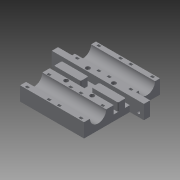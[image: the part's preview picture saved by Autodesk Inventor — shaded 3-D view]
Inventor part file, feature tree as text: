
AUTODESK INVENTOR PART (.ipt)
format: ipt  version: 2015 SP2 (Build 190223200, 223)  size: 303,616 bytes
history: native  units: mm
features: sketch x8, extrude x6, hole x2, fillet x1
ambient origin geometry x8: Origin, YZ Plane, XZ Plane, XY Plane, X Axis, Y Axis, Z Axis, Center Point
bodies: Solid1 (feature_tree)
feature tree (17):
  extrude  "Extrusion1"  Depth=70.0mm
  extrude  "Extrusion2"  Depth=13.0mm
  extrude  "Extrusion3"  Depth=22.0mm
  hole  "Hole1"  [1 undecoded]
  extrude  "Extrusion4"  Depth=45.0mm
  extrude  "Extrusion5"  Depth=13.0mm TaperAngle=0.0deg
  hole  "Hole2"  [1 undecoded]
  extrude  "Extrusion6"  Depth=3.75mm
  fillet  "Fillet1"  Radius=23.0mm
  sketch  "Sketch1"  dims[d0=85.0mm d1=70.0mm]
  sketch  "Sketch2"  dims[d2=13.0mm d3=0.0mm d4=13.0mm]
  sketch  "Sketch3"  dims[d5=5.75mm d6=22.0mm]
  sketch  "Sketch4"  dims[d7=13.0mm d8=0.0mm d9=15.0mm]
  sketch  "Sketch6"  dims[d10=15.0mm d11=45.0mm]
  sketch  "Sketch7"  dims[d12=12.0mm d13=13.0mm d14=0.0mm]
  sketch  "Sketch8"  dims[d15=24.0mm d16=20.0mm]
  sketch  "Sketch9"  dims[d17=4.0mm d18=6.0mm d19=4.0mm d20=2.0mm d21=90.0deg d22=8.0mm d23=20.594885mm d24=14.75mm d25=23.0mm d26=20.0mm d27=20.0mm d28=2.7mm d29=2.0mm d30=14.75mm d31=20.0mm d32=20.0mm d33=23.0mm d34=2.7mm d35=2.0mm d36=10.0mm d37=0.0mm d40=4.0mm d42=5.0mm d43=7.5mm d44=0.0mm d45=4.0mm d46=5.0mm d47=3.0mm d48=6.0mm d49=4.0mm d50=2.0mm d51=90.0deg d52=8.0mm d53=20.594885mm d54=2.0mm d55=0.0mm d56=1.0mm d57=3.75mm]
note: 2 required parameter values undecoded (feature->parameter linkage not recoverable at this tier; creation-order binding heuristic only, values carry confidence <= 0.55)
